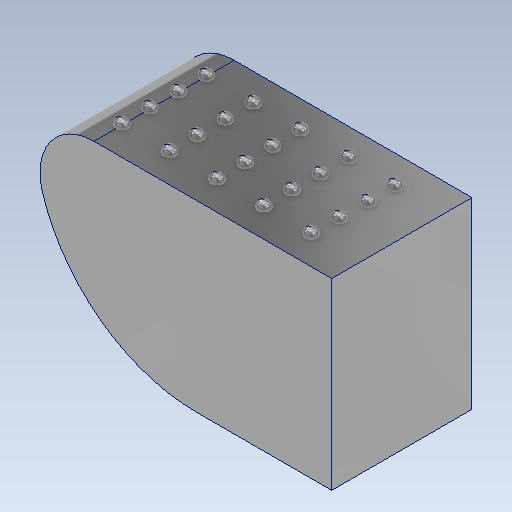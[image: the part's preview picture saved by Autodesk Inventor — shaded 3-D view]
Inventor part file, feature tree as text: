
AUTODESK INVENTOR PART (.ipt)
format: ipt  version: 2025.2 (Build 292293000, 293)  size: 3,099,136 bytes
history: native  units: mm
features: other x20, fillet x2, sketch x2, extrude x1
ambient origin geometry x8: Origin, YZ Plane, XZ Plane, XY Plane, X Axis, Y Axis, Z Axis, Center Point
bodies: Solid2 (feature_tree), Volumenkörper5 (feature_tree), Volumenkörper6 (feature_tree), Volumenkörper7 (feature_tree), Volumenkörper8 (feature_tree), Volumenkörper9 (feature_tree), Volumenkörper10 (feature_tree), Volumenkörper11 (feature_tree), Volumenkörper12 (feature_tree), Volumenkörper13 (feature_tree), Volumenkörper14 (feature_tree), Volumenkörper15 (feature_tree), Volumenkörper16 (feature_tree), Volumenkörper17 (feature_tree), Volumenkörper18 (feature_tree), Volumenkörper19 (feature_tree), Volumenkörper20 (feature_tree), Volumenkörper21 (feature_tree), Volumenkörper22 (feature_tree), Volumenkörper23 (feature_tree), Volumenkörper24 (feature_tree)
feature tree (25):
  extrude  "Extrusion2"  Depth=15.6mm
  fillet  "Fillet2"  Radius=17.0mm
  fillet  "Rundung3"  Radius=15.0mm
  sketch  "Skizze13"  dims[d105=5.0mm d106=27.5mm d114=2.6mm d115=2.6mm d116=2.6mm d122=22.039392mm d124=4.4mm d125=4.4mm d131=13.0mm d133=2.6mm d134=2.6mm d135=4.4mm d136=4.4mm d137=4.439392mm]
  other  "Form2"
  other  "Form3"
  other  "Form4"
  other  "Form5"
  other  "Form6"
  other  "Form7"
  other  "Form8"
  other  "Form9"
  other  "Form10"
  other  "Form11"
  other  "Form12"
  other  "Form13"
  other  "Form14"
  other  "Form15"
  other  "Form16"
  other  "Form17"
  other  "Form18"
  other  "Form19"
  other  "Form20"
  other  "Form21"
  sketch  "Sketch5"  dims[d56=13.0mm d57=0.0mm d67=15.6mm d97=17.0mm d98=15.0mm]
